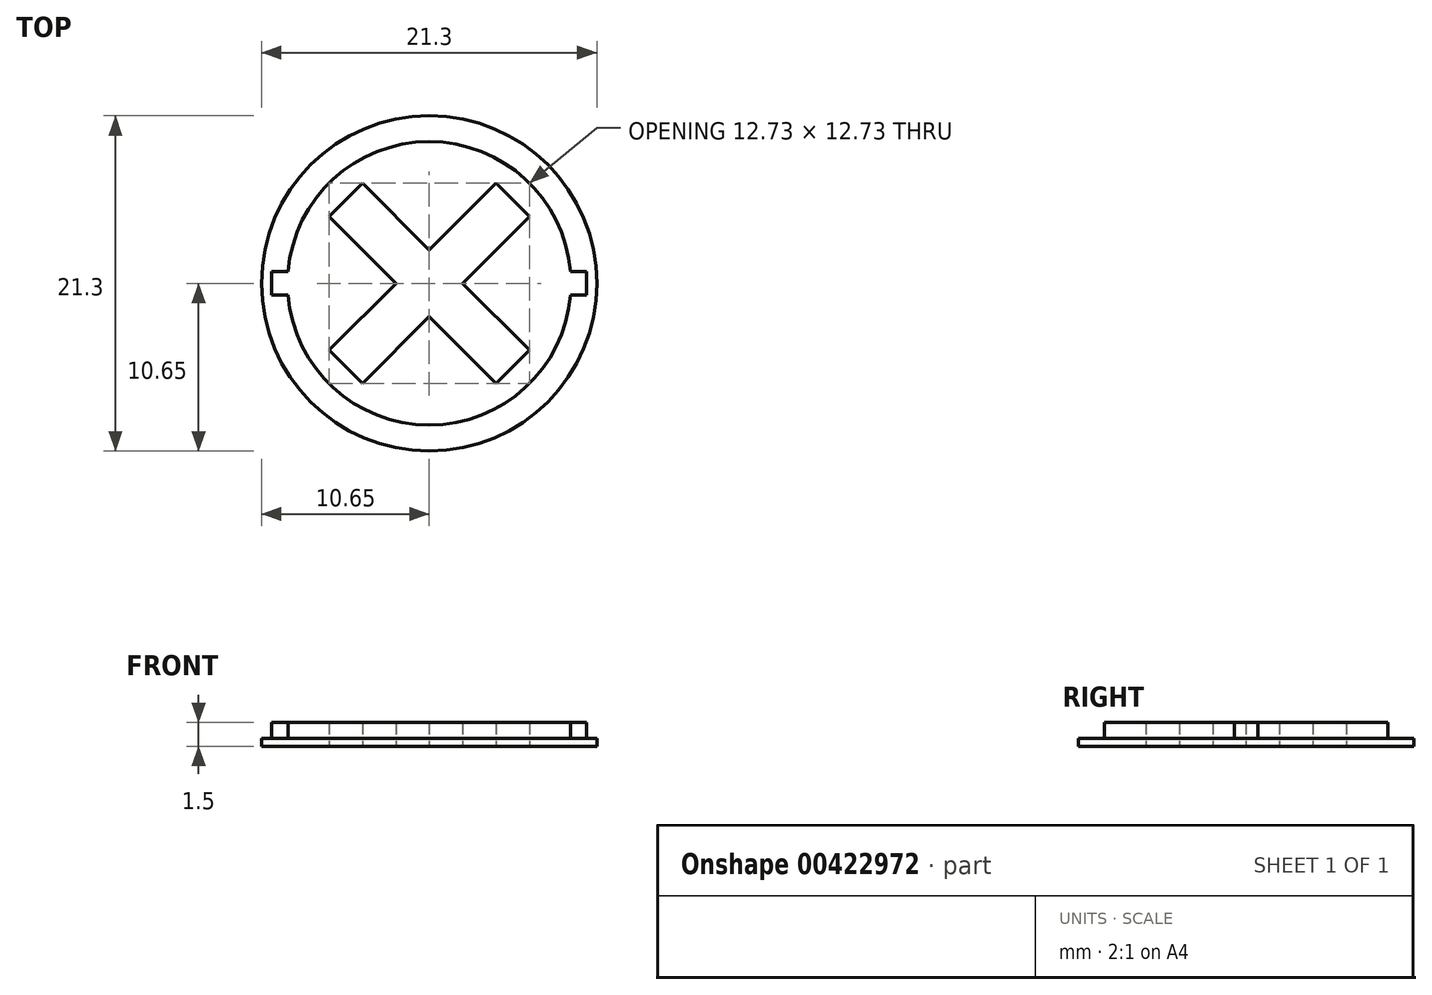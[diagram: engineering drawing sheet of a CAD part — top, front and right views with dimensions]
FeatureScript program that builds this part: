
annotation { "Feature Type Name" : "Feature", "Feature Type Description" : "" }
export const myFeature = defineFeature(function(context is Context, id is Id, definition is map)
    precondition{}
    {
        {
            var Q0;
            Q0=qCreatedBy(makeId("Top.planeOp"),FACE);
            var sketch = newSketch(context, id + "F0", { "sketchPlane" : qUnion([Q0])});
            skCircle(sketch, "E0", {"center": v(0, 0) * mm, "radius": 10.65 * mm});
            skLineSegment(sketch, "E1", {"start": v(-6.36, -4.24) * mm, "end": v(-4.24, -6.36) * mm});
            skLineSegment(sketch, "E2", {"start": v(-4.24, -6.36) * mm, "end": v(0, -2.12) * mm});
            skLineSegment(sketch, "E3", {"start": v(0, -2.12) * mm, "end": v(4.24, -6.36) * mm});
            skLineSegment(sketch, "E4", {"start": v(4.24, -6.36) * mm, "end": v(6.36, -4.24) * mm});
            skLineSegment(sketch, "E5", {"start": v(6.36, -4.24) * mm, "end": v(2.12, 0) * mm});
            skLineSegment(sketch, "E6", {"start": v(2.12, 0) * mm, "end": v(6.36, 4.24) * mm});
            skLineSegment(sketch, "E7", {"start": v(6.36, 4.24) * mm, "end": v(4.24, 6.36) * mm});
            skLineSegment(sketch, "E8", {"start": v(4.24, 6.36) * mm, "end": v(0, 2.12) * mm});
            skLineSegment(sketch, "E9", {"start": v(0, 2.12) * mm, "end": v(-4.24, 6.36) * mm});
            skLineSegment(sketch, "E10", {"start": v(-4.24, 6.36) * mm, "end": v(-6.36, 4.24) * mm});
            skLineSegment(sketch, "E11", {"start": v(-6.36, 4.24) * mm, "end": v(-2.12, 0) * mm});
            skLineSegment(sketch, "E12", {"start": v(-2.12, 0) * mm, "end": v(-6.36, -4.24) * mm});
            skLineSegment(sketch, "E13", {"start": v(-5.3, -5.3) * mm, "end": v(5.3, 5.3) * mm, "construction": true});
            skLineSegment(sketch, "E14", {"start": v(-5.3, 5.3) * mm, "end": v(5.3, -5.3) * mm, "construction": true});
            skSolve(sketch);
        }
        {
            var Q0;
            Q0=makeQuery(id+"F0.imprint","IMPRINT",FACE,{"disambiguationData":[TD([[makeQuery(id+"F0.imprint","IMPRINT",EDGE,{"derivedFrom":sQuery(id+"F0.wireOp",EDGE,"E0")}),1.0]])]});
            extrude(context, id + "F1", {"entities" : qUnion([Q0]), "depth" : 0.5 * mm});
        }
        {
            var Q0;
            Q0=makeQuery(id+"F1.opExtrude","CAP_FACE",FACE,{"disambiguationData":[OSD([sQuery(id+"F0.wireOp",EDGE,"E0"),sQuery(id+"F0.wireOp",EDGE,"E1"),sQuery(id+"F0.wireOp",EDGE,"E2"),sQuery(id+"F0.wireOp",EDGE,"E3"),sQuery(id+"F0.wireOp",EDGE,"E4"),sQuery(id+"F0.wireOp",EDGE,"E5"),sQuery(id+"F0.wireOp",EDGE,"E6"),sQuery(id+"F0.wireOp",EDGE,"E7"),sQuery(id+"F0.wireOp",EDGE,"E8"),sQuery(id+"F0.wireOp",EDGE,"E9"),sQuery(id+"F0.wireOp",EDGE,"E10"),sQuery(id+"F0.wireOp",EDGE,"E11"),sQuery(id+"F0.wireOp",EDGE,"E12")])],"isStart":false});
            var sketch = newSketch(context, id + "F2", { "sketchPlane" : qUnion([Q0])});
            skArc(sketch, "E15", {"start": v(-8.97, -0.75) * mm, "mid": v(0, -9) * mm, "end": v(8.97, -0.75) * mm});
            skLineSegment(sketch, "E16.bottom", {"start": v(-10, 0.75) * mm, "end": v(-8.97, 0.75) * mm});
            skLineSegment(sketch, "E16.top", {"start": v(-10, -0.75) * mm, "end": v(-8.97, -0.75) * mm});
            skLineSegment(sketch, "E16.left", {"start": v(-10, 0.75) * mm, "end": v(-10, -0.75) * mm});
            skLineSegment(sketch, "E16.right", {"start": v(10, 0.75) * mm, "end": v(10, -0.75) * mm});
            skLineSegment(sketch, "E17.trimOffspring", {"start": v(8.97, 0.75) * mm, "end": v(10, 0.75) * mm});
            skLineSegment(sketch, "E18.trimOffspring", {"start": v(8.97, -0.75) * mm, "end": v(10, -0.75) * mm});
            skArc(sketch, "E19.trimOffspring", {"start": v(8.97, 0.75) * mm, "mid": v(0, 9) * mm, "end": v(-8.97, 0.75) * mm});
            skSolve(sketch);
        }
        {
            var Q0;
            Q0=makeQuery(id+"F2.imprint","IMPRINT",FACE,{"disambiguationData":[TD([[makeQuery(id+"F2.imprint","IMPRINT",EDGE,{"derivedFrom":sQuery(id+"F2.wireOp",EDGE,"E15")}),1.0]])]});
            extrude(context, id + "F3", {"entities" : qUnion([Q0]), "operationType" : NewBodyOperationType.ADD, "depth" : 1 * mm});
        }
        {
            var Q0;
            Q0=makeQuery(id+"F0.imprint","IMPRINT",FACE,{"disambiguationData":[TD([[makeQuery(id+"F0.imprint","IMPRINT",EDGE,{"derivedFrom":sQuery(id+"F0.wireOp",EDGE,"E1")}),1.0]])]});
            var Q1;
            Q1=makeQuery(id+"F3.opExtrude","CAP_FACE",FACE,{"disambiguationData":[OSD([sQuery(id+"F0.wireOp",EDGE,"E1"),sQuery(id+"F0.wireOp",EDGE,"E2"),sQuery(id+"F0.wireOp",EDGE,"E3"),sQuery(id+"F0.wireOp",EDGE,"E4"),sQuery(id+"F0.wireOp",EDGE,"E5"),sQuery(id+"F0.wireOp",EDGE,"E6"),sQuery(id+"F0.wireOp",EDGE,"E7"),sQuery(id+"F0.wireOp",EDGE,"E8"),sQuery(id+"F0.wireOp",EDGE,"E9"),sQuery(id+"F0.wireOp",EDGE,"E10"),sQuery(id+"F0.wireOp",EDGE,"E11"),sQuery(id+"F0.wireOp",EDGE,"E12"),sQuery(id+"F2.wireOp",EDGE,"E15"),sQuery(id+"F2.wireOp",EDGE,"E16.bottom"),sQuery(id+"F2.wireOp",EDGE,"E16.top"),sQuery(id+"F2.wireOp",EDGE,"E16.left"),sQuery(id+"F2.wireOp",EDGE,"E16.right"),sQuery(id+"F2.wireOp",EDGE,"E17.trimOffspring"),sQuery(id+"F2.wireOp",EDGE,"E18.trimOffspring"),sQuery(id+"F2.wireOp",EDGE,"E19.trimOffspring")])],"isStart":false});
            extrude(context, id + "F4", {"entities" : qUnion([Q0]), "endBound" : BoundingType.UP_TO_SURFACE, "endBoundEntityFace" : qUnion([Q1]), "depth" : 25 * mm});
        }
    });
